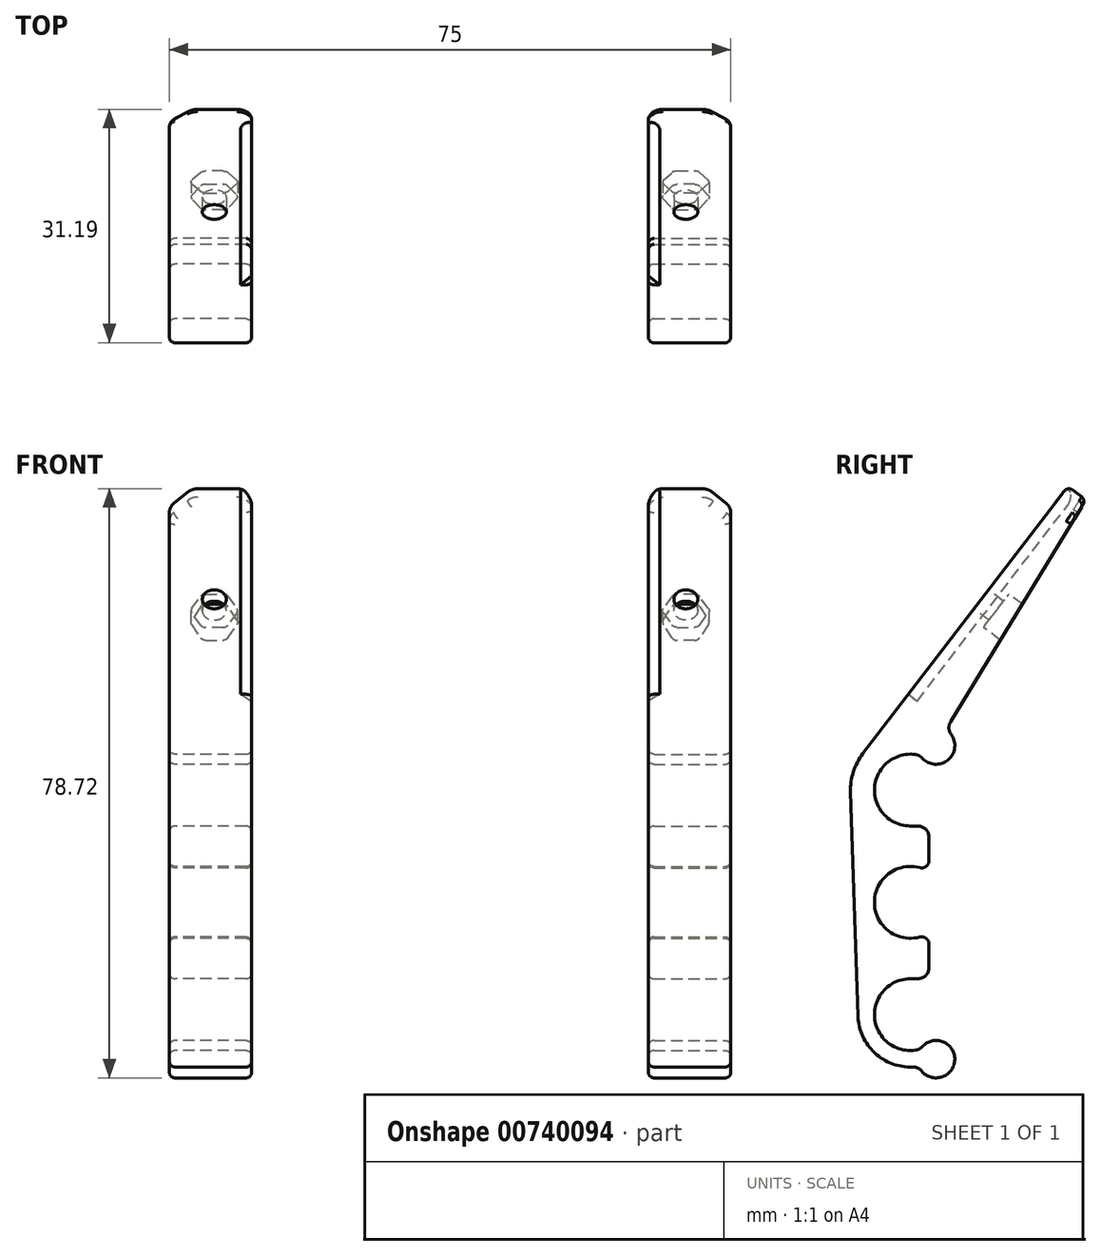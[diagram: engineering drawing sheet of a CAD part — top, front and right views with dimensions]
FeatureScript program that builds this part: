
annotation { "Feature Type Name" : "Feature", "Feature Type Description" : "" }
export const myFeature = defineFeature(function(context is Context, id is Id, definition is map)
    precondition{}
    {
        {
            var Q0;
            Q0=qCreatedBy(makeId("Right.planeOp"),FACE);
            var sketch = newSketch(context, id + "F0", { "sketchPlane" : qUnion([Q0])});
            skLineSegment(sketch, "E0", {"start": v(0, 7) * mm, "end": v(0, -37) * mm, "construction": true});
            skLineSegment(sketch, "E1", {"start": v(-7, -15) * mm, "end": v(2.5, -15) * mm, "construction": true});
            skPoint(sketch, "E2.0", {"position": v(0, -15) * mm});
            skArc(sketch, "E3", {"start": v(0.7, 4.75) * mm, "mid": v(-4.79, 0.35) * mm, "end": v(0, -4.8) * mm});
            skCircle(sketch, "E4", {"center": v(0, 0) * mm, "radius": 4.38 * mm, "construction": true});
            skLineSegment(sketch, "E5", {"start": v(0, 0) * mm, "end": v(3.44, 5.95) * mm, "construction": true});
            skArc(sketch, "E6", {"start": v(1.59, 4.27) * mm, "mid": v(5.02, 4.02) * mm, "end": v(5.44, 7.44) * mm});
            skArc(sketch, "E7", {"start": v(0.29, 7) * mm, "mid": v(-4.85, 5.05) * mm, "end": v(-7, 0) * mm, "construction": true});
            skLineSegment(sketch, "E8.0", {"start": v(-7, 0) * mm, "end": v(-7, -30) * mm, "construction": true});
            skLineSegment(sketch, "E9", {"start": v(0, -4.8) * mm, "end": v(1, -4.8) * mm});
            skLineSegment(sketch, "E10.trimOffspring", {"start": v(2.5, -6.3) * mm, "end": v(2.5, -9.4) * mm});
            skArc(sketch, "E11.filletArc", {"start": v(2.5, -6.3) * mm, "mid": v(2.06, -5.24) * mm, "end": v(1, -4.8) * mm});
            skArc(sketch, "E12.filletArc", {"start": v(1.59, 4.27) * mm, "mid": v(1.18, 4.59) * mm, "end": v(0.7, 4.75) * mm});
            skArc(sketch, "E13.filletArc", {"start": v(0.29, 7) * mm, "mid": v(0.96, 7.12) * mm, "end": v(1.5, 7.54) * mm, "construction": true});
            skPoint(sketch, "E14.orphan", {"position": v(-7, -15) * mm});
            skLineSegment(sketch, "E15.MirrorCS", {"start": v(0, -25.2) * mm, "end": v(1, -25.2) * mm});
            skArc(sketch, "E16.MirrorCS", {"start": v(1.59, -34.27) * mm, "mid": v(1.18, -34.59) * mm, "end": v(0.7, -34.75) * mm});
            skArc(sketch, "E17.MirrorCS", {"start": v(0.29, -37) * mm, "mid": v(0.96, -37.12) * mm, "end": v(1.5, -37.54) * mm});
            skArc(sketch, "E18.MirrorCS", {"start": v(0.29, -37) * mm, "mid": v(-4.85, -35.05) * mm, "end": v(-7, -30) * mm});
            skCircle(sketch, "E19.MirrorC", {"center": v(0, -30) * mm, "radius": 4.38 * mm, "construction": true});
            skArc(sketch, "E20.MirrorCS", {"start": v(0.7, -34.75) * mm, "mid": v(-4.79, -30.35) * mm, "end": v(0, -25.2) * mm});
            skArc(sketch, "E21.MirrorCS", {"start": v(1.59, -34.27) * mm, "mid": v(5.94, -36.02) * mm, "end": v(1.5, -37.54) * mm});
            skArc(sketch, "E22.MirrorCS", {"start": v(2.5, -23.7) * mm, "mid": v(2.06, -24.76) * mm, "end": v(1, -25.2) * mm});
            skArc(sketch, "E23", {"start": v(-6.35, 4.87) * mm, "mid": v(-7.62, 2.44) * mm, "end": v(-8, -0.27) * mm});
            skLineSegment(sketch, "E24", {"start": v(-8, -0.27) * mm, "end": v(-7, -30.23) * mm});
            skArc(sketch, "E25", {"start": v(5.44, 7.44) * mm, "mid": v(3.5, 8.45) * mm, "end": v(1.5, 7.54) * mm, "construction": true});
            skLineSegment(sketch, "E26", {"start": v(-6.35, 4.87) * mm, "end": v(0, 0) * mm, "construction": true});
            skLineSegment(sketch, "E27", {"start": v(4.37, 0) * mm, "end": v(-8, 0) * mm, "construction": true});
            skLineSegment(sketch, "E28", {"start": v(-6.35, 4.87) * mm, "end": v(21.05, 40.57) * mm});
            skLineSegment(sketch, "E29.0", {"start": v(21.05, 40.57) * mm, "end": v(23.43, 38.74) * mm});
            skLineSegment(sketch, "E30", {"start": v(23.43, 38.74) * mm, "end": v(5.37, 9.12) * mm});
            skArc(sketch, "E31.filletArc", {"start": v(5.37, 9.12) * mm, "mid": v(5.15, 8.27) * mm, "end": v(5.44, 7.44) * mm});
            skArc(sketch, "E32", {"start": v(1.24, -10.36) * mm, "mid": v(-4.8, -15) * mm, "end": v(1.24, -19.64) * mm});
            skLineSegment(sketch, "E33.trimOffspring", {"start": v(2.5, -20.6) * mm, "end": v(2.5, -23.7) * mm});
            skArc(sketch, "E34.filletArc", {"start": v(1.24, -10.36) * mm, "mid": v(2.1, -10.2) * mm, "end": v(2.5, -9.4) * mm});
            skArc(sketch, "E35.filletArc", {"start": v(2.5, -20.6) * mm, "mid": v(2.1, -19.8) * mm, "end": v(1.24, -19.64) * mm});
            skSolve(sketch);
        }
        {
            var Q0;
            Q0=makeQuery(id+"F0.imprint","IMPRINT",FACE,{"disambiguationData":[TD([[makeQuery(id+"F0.imprint","IMPRINT",EDGE,{"derivedFrom":sQuery(id+"F0.wireOp",EDGE,"E3")}),-1.0]])]});
            extrude(context, id + "F1", {"entities" : qUnion([Q0]), "depth" : 11 * mm, "offsetDistance" : 25 * mm});
        }
        {
            var Q0;
            Q0=makeQuery(id+"F1.opExtrude","SWEPT_FACE",FACE,{"disambiguationData":[OSD([sQuery(id+"F0.wireOp",EDGE,"E28")])]});
            var sketch = newSketch(context, id + "F2", { "sketchPlane" : qUnion([Q0])});
            skCircle(sketch, "E36", {"center": v(6, 26) * mm, "radius": 1.6 * mm});
            skSolve(sketch);
        }
        {
            var Q0;
            Q0 = qSketchRegion(id + "F2", true);
            extrude(context, id + "F3", {"entities" : qUnion([Q0]), "operationType" : NewBodyOperationType.REMOVE, "oppositeDirection" : true, "depth" : 2.5 * mm, "offsetDistance" : 25 * mm});
        }
        {
            var Q0;
            Q0=makeQuery(id+"F3.boolean.opBoolean","COPY",FACE,{"derivedFrom":makeQuery(id+"F3.opExtrude","CAP_FACE",FACE,{"disambiguationData":[OSD([sQuery(id+"F2.wireOp",EDGE,"E36")])],"isStart":false})});
            var sketch = newSketch(context, id + "F4", { "sketchPlane" : qUnion([Q0])});
            skCircle(sketch, "E37.cCircle", {"center": v(6, 26) * mm, "radius": 2.8 * mm, "construction": true});
            skLineSegment(sketch, "E37.0", {"start": v(7.18, 23.2) * mm, "end": v(4.82, 23.2) * mm});
            skLineSegment(sketch, "E37.1", {"start": v(4.17, 23.58) * mm, "end": v(2.98, 25.63) * mm});
            skLineSegment(sketch, "E37.2", {"start": v(2.98, 26.38) * mm, "end": v(4.17, 28.42) * mm});
            skLineSegment(sketch, "E37.3", {"start": v(4.82, 28.8) * mm, "end": v(7.18, 28.8) * mm});
            skLineSegment(sketch, "E37.4", {"start": v(7.83, 28.42) * mm, "end": v(9.02, 26.38) * mm});
            skLineSegment(sketch, "E37.5", {"start": v(9.02, 25.63) * mm, "end": v(7.83, 23.58) * mm});
            skPoint(sketch, "E37.0.midPoint", {"position": v(6, 23.2) * mm});
            skPoint(sketch, "E38.visualSharp", {"position": v(7.62, 28.8) * mm});
            skArc(sketch, "E38.filletArc", {"start": v(7.83, 28.43) * mm, "mid": v(7.56, 28.7) * mm, "end": v(7.18, 28.8) * mm});
            skPoint(sketch, "E39.visualSharp", {"position": v(4.38, 28.8) * mm});
            skArc(sketch, "E39.filletArc", {"start": v(4.82, 28.8) * mm, "mid": v(4.44, 28.7) * mm, "end": v(4.17, 28.43) * mm});
            skPoint(sketch, "E40.visualSharp", {"position": v(2.77, 26) * mm});
            skArc(sketch, "E40.filletArc", {"start": v(2.98, 26.38) * mm, "mid": v(2.88, 26) * mm, "end": v(2.98, 25.63) * mm});
            skPoint(sketch, "E41.visualSharp", {"position": v(4.38, 23.2) * mm});
            skArc(sketch, "E41.filletArc", {"start": v(4.17, 23.58) * mm, "mid": v(4.44, 23.3) * mm, "end": v(4.82, 23.2) * mm});
            skPoint(sketch, "E42.visualSharp", {"position": v(7.62, 23.2) * mm});
            skArc(sketch, "E42.filletArc", {"start": v(7.18, 23.2) * mm, "mid": v(7.56, 23.3) * mm, "end": v(7.83, 23.58) * mm});
            skPoint(sketch, "E43.visualSharp", {"position": v(9.23, 26) * mm});
            skArc(sketch, "E43.filletArc", {"start": v(9.02, 25.63) * mm, "mid": v(9.12, 26) * mm, "end": v(9.02, 26.38) * mm});
            skSolve(sketch);
        }
        {
            var Q0;
            Q0 = qSketchRegion(id + "F4", true);
            extrude(context, id + "F5", {"entities" : qUnion([Q0]), "operationType" : NewBodyOperationType.REMOVE, "endBound" : BoundingType.THROUGH_ALL, "oppositeDirection" : true, "depth" : 25 * mm, "offsetDistance" : 25 * mm});
        }
        {
            var Q0;
            Q0=makeQuery(id+"F1.opExtrude","SWEPT_FACE",FACE,{"disambiguationData":[OSD([sQuery(id+"F0.wireOp",EDGE,"E29.0")])]});
            var sketch = newSketch(context, id + "F6", { "sketchPlane" : qUnion([Q0])});
            skLineSegment(sketch, "E44.0", {"start": v(11, -8) * mm, "end": v(9.5, -8) * mm});
            skLineSegment(sketch, "E44.1", {"start": v(11, -8) * mm, "end": v(11, -6.5) * mm});
            skLineSegment(sketch, "E45", {"start": v(9.5, -8) * mm, "end": v(11, -6.5) * mm});
            skSolve(sketch);
        }
        {
            var Q0;
            Q0 = qSketchRegion(id + "F6", true);
            extrude(context, id + "F7", {"entities" : qUnion([Q0]), "operationType" : NewBodyOperationType.REMOVE, "oppositeDirection" : true, "depth" : 35 * mm, "offsetDistance" : 25 * mm});
        }
        {
            var Q0;
            Q0=makeQuery(id+"F1.opExtrude","CAP_EDGE",EDGE,{"disambiguationData":[OSD([sQuery(id+"F0.wireOp",EDGE,"E29.0")])],"isStart":true});
            chamfer(context, id + "F8", {"entities" : qUnion([Q0]), "width" : 3 * mm, "tangentPropagation" : true});
        }
        {
            var Q0;
            {var subQ0=sQuery(id+"F0.wireOp",EDGE,"E29.0");Q0=makeQuery(id+"F8.opChamfer","BLEND_EDGE",EDGE,{"blendedFrom":[makeQuery(id+"F1.opExtrude","CAP_EDGE",EDGE,{"disambiguationData":[OSD([subQ0])],"isStart":true}),makeQuery(id+"F1.opExtrude","CAP_FACE",FACE,{"disambiguationData":[OSD([sQuery(id+"F0.wireOp",EDGE,"E3"),sQuery(id+"F0.wireOp",EDGE,"E6"),sQuery(id+"F0.wireOp",EDGE,"E9"),sQuery(id+"F0.wireOp",EDGE,"E10.trimOffspring"),sQuery(id+"F0.wireOp",EDGE,"E11.filletArc"),sQuery(id+"F0.wireOp",EDGE,"E12.filletArc"),sQuery(id+"F0.wireOp",EDGE,"E15.MirrorCS"),sQuery(id+"F0.wireOp",EDGE,"E16.MirrorCS"),sQuery(id+"F0.wireOp",EDGE,"E17.MirrorCS"),sQuery(id+"F0.wireOp",EDGE,"E18.MirrorCS"),sQuery(id+"F0.wireOp",EDGE,"E20.MirrorCS"),sQuery(id+"F0.wireOp",EDGE,"E21.MirrorCS"),sQuery(id+"F0.wireOp",EDGE,"E22.MirrorCS"),sQuery(id+"F0.wireOp",EDGE,"E23"),sQuery(id+"F0.wireOp",EDGE,"E24"),sQuery(id+"F0.wireOp",EDGE,"E28"),subQ0,sQuery(id+"F0.wireOp",EDGE,"E30"),sQuery(id+"F0.wireOp",EDGE,"E31.filletArc"),sQuery(id+"F0.wireOp",EDGE,"E32"),sQuery(id+"F0.wireOp",EDGE,"E33.trimOffspring"),sQuery(id+"F0.wireOp",EDGE,"E34.filletArc"),sQuery(id+"F0.wireOp",EDGE,"E35.filletArc")])],"isStart":true})],"blendedInto":[makeQuery(id+"F1.opExtrude","CAP_FACE",FACE,{"disambiguationData":[OSD([sQuery(id+"F0.wireOp",EDGE,"E3"),sQuery(id+"F0.wireOp",EDGE,"E6"),sQuery(id+"F0.wireOp",EDGE,"E9"),sQuery(id+"F0.wireOp",EDGE,"E10.trimOffspring"),sQuery(id+"F0.wireOp",EDGE,"E11.filletArc"),sQuery(id+"F0.wireOp",EDGE,"E12.filletArc"),sQuery(id+"F0.wireOp",EDGE,"E15.MirrorCS"),sQuery(id+"F0.wireOp",EDGE,"E16.MirrorCS"),sQuery(id+"F0.wireOp",EDGE,"E17.MirrorCS"),sQuery(id+"F0.wireOp",EDGE,"E18.MirrorCS"),sQuery(id+"F0.wireOp",EDGE,"E20.MirrorCS"),sQuery(id+"F0.wireOp",EDGE,"E21.MirrorCS"),sQuery(id+"F0.wireOp",EDGE,"E22.MirrorCS"),sQuery(id+"F0.wireOp",EDGE,"E23"),sQuery(id+"F0.wireOp",EDGE,"E24"),sQuery(id+"F0.wireOp",EDGE,"E28"),subQ0,sQuery(id+"F0.wireOp",EDGE,"E30"),sQuery(id+"F0.wireOp",EDGE,"E31.filletArc"),sQuery(id+"F0.wireOp",EDGE,"E32"),sQuery(id+"F0.wireOp",EDGE,"E33.trimOffspring"),sQuery(id+"F0.wireOp",EDGE,"E34.filletArc"),sQuery(id+"F0.wireOp",EDGE,"E35.filletArc")])],"isStart":true})]});}
            var Q1;
            {var subQ0=sQuery(id+"F0.wireOp",EDGE,"E29.0");Q1=makeQuery(id+"F8.opChamfer","BLEND_EDGE",EDGE,{"blendedFrom":[makeQuery(id+"F1.opExtrude","CAP_EDGE",EDGE,{"disambiguationData":[OSD([subQ0])],"isStart":true}),makeQuery(id+"F1.opExtrude","SWEPT_FACE",FACE,{"disambiguationData":[OSD([subQ0])]})],"blendedInto":[makeQuery(id+"F1.opExtrude","SWEPT_FACE",FACE,{"disambiguationData":[OSD([subQ0])]})]});}
            var Q2;
            Q2=makeQuery(id+"F1.opExtrude","CAP_EDGE",EDGE,{"disambiguationData":[OSD([sQuery(id+"F0.wireOp",EDGE,"E29.0")])],"isStart":false});
            fillet(context, id + "F9", {"entities" : qUnion([Q0, Q1, Q2]), "radius" : 2 * mm, "tangentPropagation" : true, "allowEdgeOverflow" : false});
        }
        {
            var Q0;
            Q0=makeQuery(id+"F1.opExtrude","CAP_EDGE",EDGE,{"disambiguationData":[OSD([sQuery(id+"F0.wireOp",EDGE,"E24")])],"isStart":true});
            fillet(context, id + "F10", {"entities" : qUnion([Q0]), "radius" : 0.75 * mm, "tangentPropagation" : true, "allowEdgeOverflow" : false});
        }
        {
            var Q0;
            Q0=makeQuery(id+"F1.opExtrude","SWEPT_BODY",BODY,{"disambiguationData":[OSD([sQuery(id+"F0.wireOp",EDGE,"E3"),sQuery(id+"F0.wireOp",EDGE,"E6"),sQuery(id+"F0.wireOp",EDGE,"E9"),sQuery(id+"F0.wireOp",EDGE,"E10.trimOffspring"),sQuery(id+"F0.wireOp",EDGE,"E11.filletArc"),sQuery(id+"F0.wireOp",EDGE,"E12.filletArc"),sQuery(id+"F0.wireOp",EDGE,"E15.MirrorCS"),sQuery(id+"F0.wireOp",EDGE,"E16.MirrorCS"),sQuery(id+"F0.wireOp",EDGE,"E17.MirrorCS"),sQuery(id+"F0.wireOp",EDGE,"E18.MirrorCS"),sQuery(id+"F0.wireOp",EDGE,"E20.MirrorCS"),sQuery(id+"F0.wireOp",EDGE,"E21.MirrorCS"),sQuery(id+"F0.wireOp",EDGE,"E22.MirrorCS"),sQuery(id+"F0.wireOp",EDGE,"E23"),sQuery(id+"F0.wireOp",EDGE,"E24"),sQuery(id+"F0.wireOp",EDGE,"E28"),sQuery(id+"F0.wireOp",EDGE,"E29.0"),sQuery(id+"F0.wireOp",EDGE,"E30"),sQuery(id+"F0.wireOp",EDGE,"E31.filletArc"),sQuery(id+"F0.wireOp",EDGE,"E32"),sQuery(id+"F0.wireOp",EDGE,"E33.trimOffspring"),sQuery(id+"F0.wireOp",EDGE,"E34.filletArc"),sQuery(id+"F0.wireOp",EDGE,"E35.filletArc")])]});
            var Q1;
            Q1=qCreatedBy(makeId("Right.planeOp"),FACE);
            mirror(context, id + "F11", {"entities" : qUnion([Q0]), "mirrorPlane" : qUnion([Q1])});
        }
        {
            var Q0;
            Q0=makeQuery(id+"F11.opPattern","COPY",BODY,{"derivedFrom":makeQuery(id+"F1.opExtrude","SWEPT_BODY",BODY,{"disambiguationData":[OSD([sQuery(id+"F0.wireOp",EDGE,"E3"),sQuery(id+"F0.wireOp",EDGE,"E6"),sQuery(id+"F0.wireOp",EDGE,"E9"),sQuery(id+"F0.wireOp",EDGE,"E10.trimOffspring"),sQuery(id+"F0.wireOp",EDGE,"E11.filletArc"),sQuery(id+"F0.wireOp",EDGE,"E12.filletArc"),sQuery(id+"F0.wireOp",EDGE,"E15.MirrorCS"),sQuery(id+"F0.wireOp",EDGE,"E16.MirrorCS"),sQuery(id+"F0.wireOp",EDGE,"E17.MirrorCS"),sQuery(id+"F0.wireOp",EDGE,"E18.MirrorCS"),sQuery(id+"F0.wireOp",EDGE,"E20.MirrorCS"),sQuery(id+"F0.wireOp",EDGE,"E21.MirrorCS"),sQuery(id+"F0.wireOp",EDGE,"E22.MirrorCS"),sQuery(id+"F0.wireOp",EDGE,"E23"),sQuery(id+"F0.wireOp",EDGE,"E24"),sQuery(id+"F0.wireOp",EDGE,"E28"),sQuery(id+"F0.wireOp",EDGE,"E29.0"),sQuery(id+"F0.wireOp",EDGE,"E30"),sQuery(id+"F0.wireOp",EDGE,"E31.filletArc"),sQuery(id+"F0.wireOp",EDGE,"E32"),sQuery(id+"F0.wireOp",EDGE,"E33.trimOffspring"),sQuery(id+"F0.wireOp",EDGE,"E34.filletArc"),sQuery(id+"F0.wireOp",EDGE,"E35.filletArc")])]}),"instanceName":"1"});
            transform(context, id + "F12", {"entities" : qUnion([Q0]), "transformType" : TransformType.TRANSLATION_3D, "dx" : 75 * mm, "dy" : 0 * mm, "dz" : 0 * mm, "makeCopy" : false});
        }
    });
